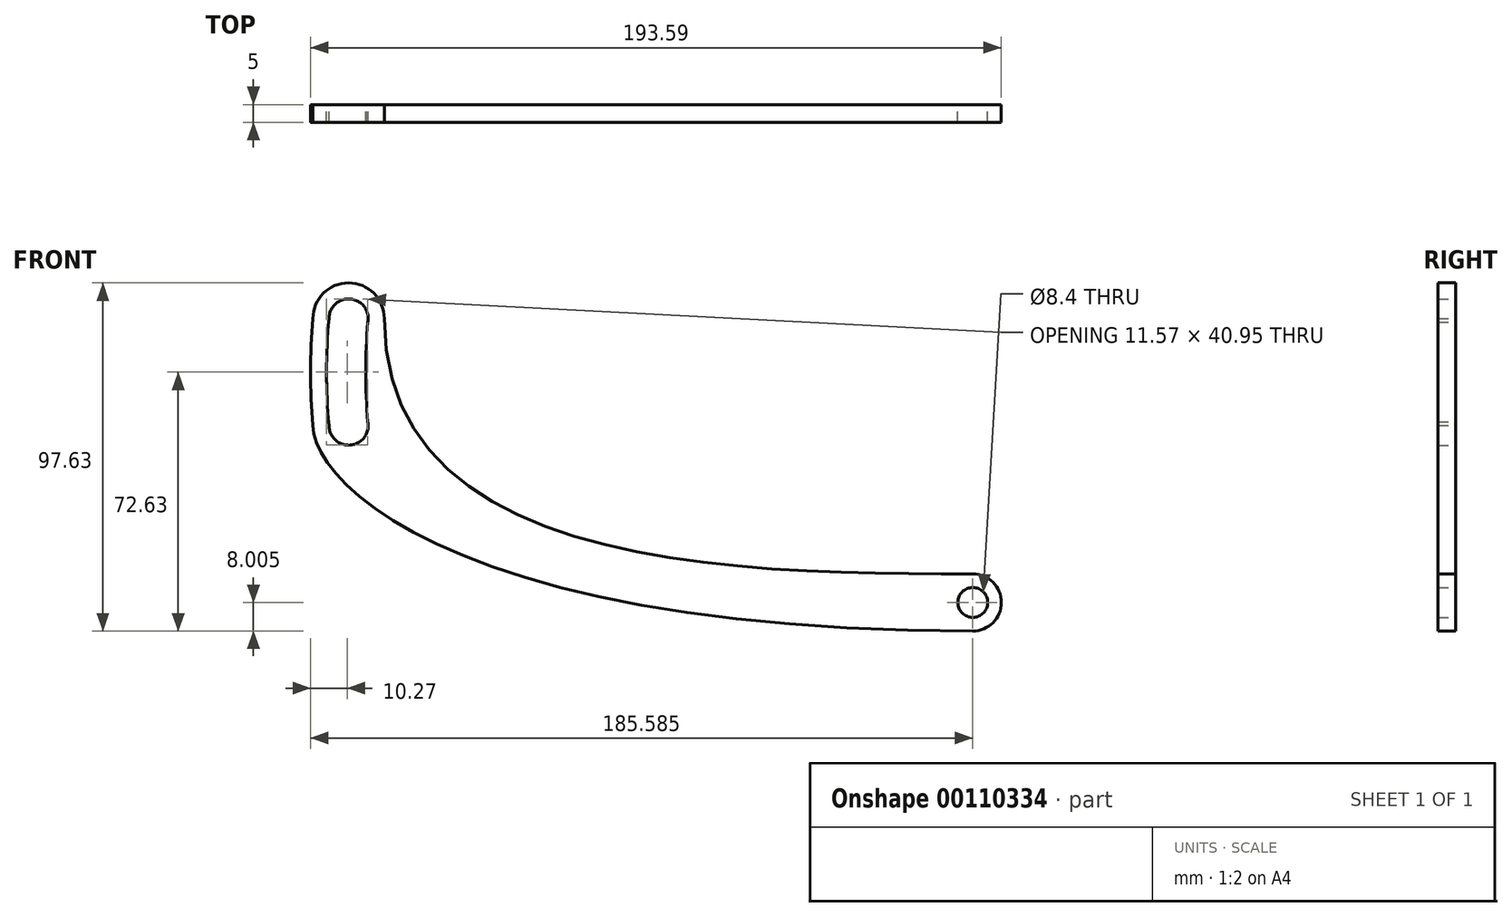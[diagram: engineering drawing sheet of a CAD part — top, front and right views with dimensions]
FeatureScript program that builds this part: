
annotation { "Feature Type Name" : "Feature", "Feature Type Description" : "" }
export const myFeature = defineFeature(function(context is Context, id is Id, definition is map)
    precondition{}
    {
        {
            var Q0;
            Q0=qCreatedBy(makeId("Front.planeOp"),FACE);
            var sketch = newSketch(context, id + "F0", { "sketchPlane" : qUnion([Q0])});
            skCircle(sketch, "E0", {"center": v(0, 0) * mm, "radius": 5.25 * mm});
            skCircle(sketch, "E1", {"center": v(12.13, -64.62) * mm, "radius": 3.43 * mm});
            skCircle(sketch, "E2", {"center": v(-162.81, 15) * mm, "radius": 5.5 * mm});
            skCircle(sketch, "E3", {"center": v(-162.81, -15) * mm, "radius": 5.5 * mm});
            skCircle(sketch, "E4", {"center": v(-79.03, 25.37) * mm, "radius": 62.5 * mm});
            skSolve(sketch);
        }
        {
            var Q0;
            Q0=qCreatedBy(makeId("Front.planeOp"),FACE);
            var sketch = newSketch(context, id + "F1", { "sketchPlane" : qUnion([Q0])});
            skPoint(sketch, "E5.0", {"position": v(12.13, -64.62) * mm});
            skPoint(sketch, "E6.0", {"position": v(-162.81, 15) * mm});
            skPoint(sketch, "E6.1", {"position": v(-162.81, -15) * mm});
            skCircle(sketch, "E7.0", {"center": v(-79.03, 25.37) * mm, "radius": 62.5 * mm, "construction": true});
            skArc(sketch, "E8", {"start": v(-152.81, 15) * mm, "mid": v(-162.81, 25) * mm, "end": v(-172.81, 15) * mm});
            skArc(sketch, "E9", {"start": v(12.13, -72.62) * mm, "mid": v(20.13, -64.62) * mm, "end": v(12.13, -56.62) * mm});
            skLineSegment(sketch, "E10", {"start": v(-162.81, -15) * mm, "end": v(-179.03, -15) * mm});
            skLineSegment(sketch, "E11", {"start": v(-179.03, -15) * mm, "end": v(-149.8, -15) * mm, "construction": true});
            skLineSegment(sketch, "E12", {"start": v(-162.81, 15) * mm, "end": v(-185.71, 15) * mm, "construction": true});
            skLineSegment(sketch, "E13", {"start": v(-185.71, 15) * mm, "end": v(-121.84, 15) * mm, "construction": true});
            skArc(sketch, "E14.0", {"start": v(-157.4, 14) * mm, "mid": v(-162.3, 20.48) * mm, "end": v(-168.31, 15) * mm});
            skArc(sketch, "E14.1", {"start": v(-168.31, -15) * mm, "mid": v(-162.3, -20.48) * mm, "end": v(-157.4, -14) * mm});
            skArc(sketch, "E15", {"start": v(-157.31, 15) * mm, "mid": v(-158.02, 0) * mm, "end": v(-157.31, -15) * mm});
            skArc(sketch, "E16", {"start": v(-168.31, -15) * mm, "mid": v(-168.98, 0) * mm, "end": v(-168.31, 15) * mm});
            skCircle(sketch, "E17.0", {"center": v(-79.03, 25.37) * mm, "radius": 72.5 * mm, "construction": true});
            skFitSpline(sketch, "E18", {"points": [v(-152.81, 15) * mm, v(12.13, -56.62) * mm], "startDerivative": vector(0, -211.58) * mm, "endDerivative": vector(199.69, 0) * mm});
            skArc(sketch, "E19", {"start": v(-172.81, 15) * mm, "mid": v(-173.46, 0) * mm, "end": v(-172.81, -15) * mm});
            skFitSpline(sketch, "E20", {"points": [v(-172.81, -15) * mm, v(12.13, -72.62) * mm], "startDerivative": vector(0, -48.36) * mm, "endDerivative": vector(433.31, 0) * mm});
            skCircle(sketch, "E21", {"center": v(12.13, -64.62) * mm, "radius": 4.2 * mm});
            skSolve(sketch);
        }
        {
            var Q0;
            Q0=makeQuery(id+"F1.imprint","IMPRINT",FACE,{"disambiguationData":[TD([[makeQuery(id+"F1.imprint","IMPRINT",EDGE,{"derivedFrom":sQuery(id+"F1.wireOp",EDGE,"E8")}),1.0]])]});
            extrude(context, id + "F2", {"entities" : qUnion([Q0]), "depth" : 5 * mm});
        }
    });
